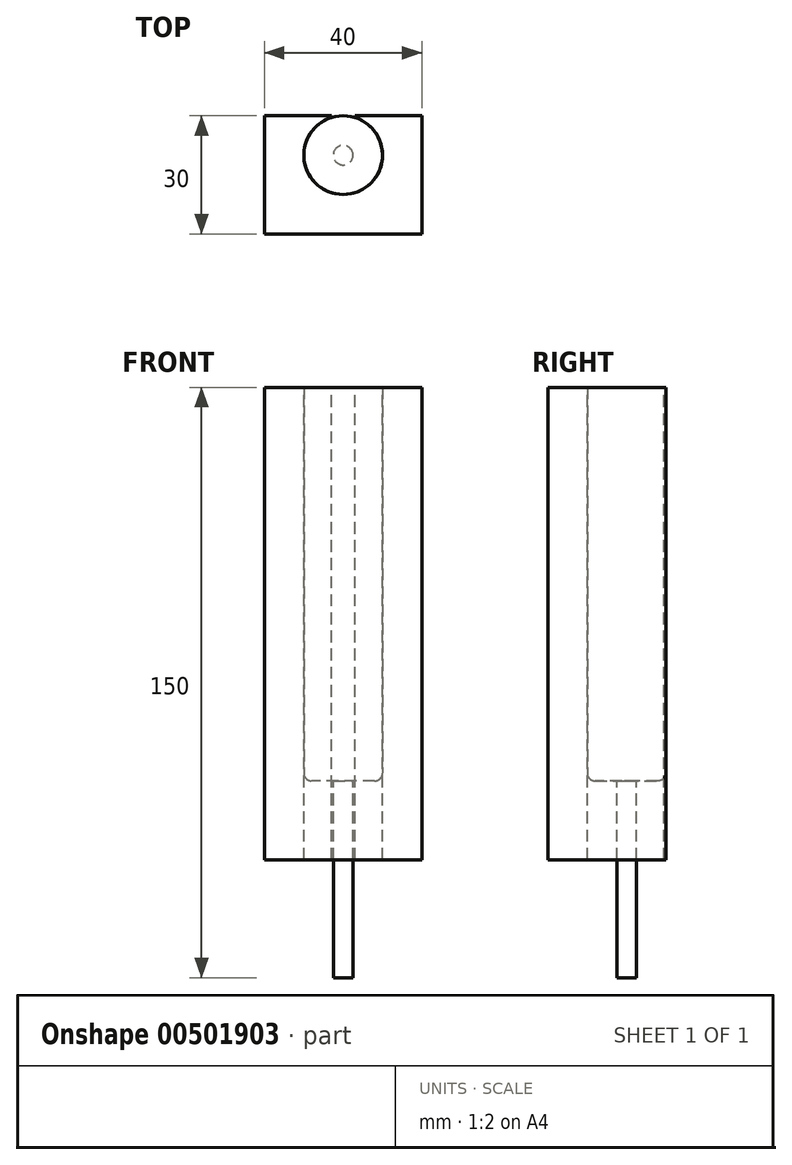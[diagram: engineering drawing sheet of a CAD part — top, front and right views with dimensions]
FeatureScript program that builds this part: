
annotation { "Feature Type Name" : "Feature", "Feature Type Description" : "" }
export const myFeature = defineFeature(function(context is Context, id is Id, definition is map)
    precondition{}
    {
        {
            var Q0;
            Q0=qCreatedBy(makeId("Top.planeOp"),FACE);
            var sketch = newSketch(context, id + "F0", { "sketchPlane" : qUnion([Q0])});
            skCircle(sketch, "E0", {"center": v(0, 0) * mm, "radius": 10 * mm});
            skSolve(sketch);
        }
        {
            var Q0;
            Q0=makeQuery(id+"F0.imprint","IMPRINT",FACE,{"disambiguationData":[TD([[makeQuery(id+"F0.imprint","IMPRINT",EDGE,{"derivedFrom":sQuery(id+"F0.wireOp",EDGE,"E0")}),1.0]])]});
            extrude(context, id + "F1", {"entities" : qUnion([Q0]), "depth" : 100 * mm});
        }
        {
            var Q0;
            Q0=makeQuery(id+"F1.opExtrude","CAP_FACE",FACE,{"disambiguationData":[OSD([sQuery(id+"F0.wireOp",EDGE,"E0")])],"isStart":true});
            var sketch = newSketch(context, id + "F2", { "sketchPlane" : qUnion([Q0])});
            skCircle(sketch, "E1", {"center": v(0, 0) * mm, "radius": 2.5 * mm});
            skSolve(sketch);
        }
        {
            var Q0;
            Q0=makeQuery(id+"F2.imprint","IMPRINT",FACE,{"disambiguationData":[TD([[makeQuery(id+"F2.imprint","IMPRINT",EDGE,{"derivedFrom":sQuery(id+"F2.wireOp",EDGE,"E1")}),1.0]])]});
            extrude(context, id + "F3", {"entities" : qUnion([Q0]), "operationType" : NewBodyOperationType.ADD, "depth" : 50 * mm});
        }
        {
            var Q0;
            Q0=makeQuery(id+"F1.opExtrude","CAP_EDGE",EDGE,{"disambiguationData":[OSD([sQuery(id+"F0.wireOp",EDGE,"E0")])],"isStart":true});
            fillet(context, id + "F4", {"entities" : qUnion([Q0]), "radius" : 2 * mm, "tangentPropagation" : true, "allowEdgeOverflow" : false});
        }
        {
            var Q0;
            Q0=makeQuery(id+"F1.opExtrude","CAP_FACE",FACE,{"disambiguationData":[OSD([sQuery(id+"F0.wireOp",EDGE,"E0")])],"isStart":false});
            var sketch = newSketch(context, id + "F5", { "sketchPlane" : qUnion([Q0])});
            skLineSegment(sketch, "E2.bottom", {"start": v(20, -20) * mm, "end": v(-20, -20) * mm});
            skLineSegment(sketch, "E2.left", {"start": v(20, -20) * mm, "end": v(20, 10) * mm});
            skLineSegment(sketch, "E2.right", {"start": v(-20, -20) * mm, "end": v(-20, 10) * mm});
            skPoint(sketch, "E2.middle", {"position": v(0, 0) * mm});
            skLineSegment(sketch, "E3", {"start": v(-20, 10) * mm, "end": v(-3, 10) * mm});
            skPoint(sketch, "E4.orphan", {"position": v(-20, 20) * mm});
            skPoint(sketch, "E5.orphan", {"position": v(20, 20) * mm});
            skArc(sketch, "E6.0", {"start": v(-3, 9.54) * mm, "mid": v(0, -10) * mm, "end": v(3, 9.54) * mm});
            skLineSegment(sketch, "E7", {"start": v(-3, 10) * mm, "end": v(-3, 9.54) * mm});
            skLineSegment(sketch, "E8", {"start": v(3, 10) * mm, "end": v(3, 9.54) * mm});
            skLineSegment(sketch, "E9.trimOffspring", {"start": v(3, 10) * mm, "end": v(20, 10) * mm});
            skSolve(sketch);
        }
        {
            var Q0;
            Q0=makeQuery(id+"F5.imprint","IMPRINT",FACE,{"disambiguationData":[TD([[makeQuery(id+"F5.imprint","IMPRINT",EDGE,{"derivedFrom":sQuery(id+"F5.wireOp",EDGE,"E2.bottom")}),-1.0]])]});
            extrude(context, id + "F6", {"entities" : qUnion([Q0]), "oppositeDirection" : true, "depth" : 120 * mm});
        }
    });
